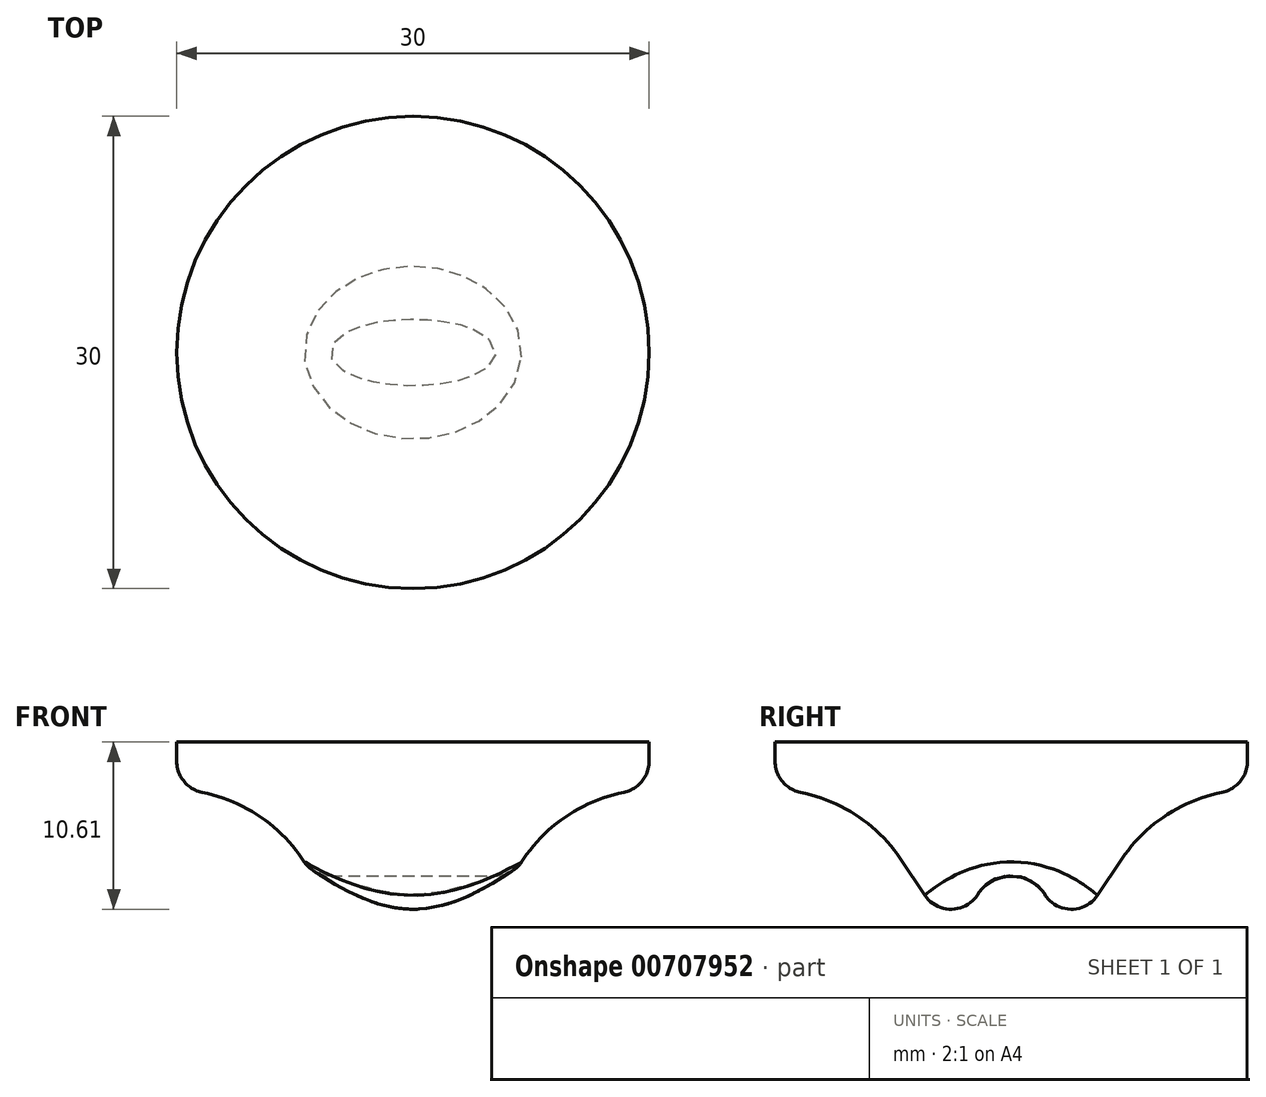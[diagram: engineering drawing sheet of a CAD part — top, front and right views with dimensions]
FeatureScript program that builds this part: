
annotation { "Feature Type Name" : "Feature", "Feature Type Description" : "" }
export const myFeature = defineFeature(function(context is Context, id is Id, definition is map)
    precondition{}
    {
        {
            var Q0;
            Q0=qCreatedBy(makeId("Front.planeOp"),FACE);
            var sketch = newSketch(context, id + "F0", { "sketchPlane" : qUnion([Q0])});
            skLineSegment(sketch, "E0", {"start": v(0, 0) * mm, "end": v(-15, 0) * mm});
            skLineSegment(sketch, "E1", {"start": v(-15, 0) * mm, "end": v(-15, -3) * mm});
            skLineSegment(sketch, "E2", {"start": v(-15, -3) * mm, "end": v(-10, -3) * mm});
            skLineSegment(sketch, "E3", {"start": v(-10, -3) * mm, "end": v(-2.62, -13.99) * mm});
            skLineSegment(sketch, "E4", {"start": v(0, -13.99) * mm, "end": v(-2.62, -13.99) * mm});
            skLineSegment(sketch, "E5", {"start": v(0, -13.99) * mm, "end": v(0, 0) * mm});
            skSolve(sketch);
        }
        {
            var Q0;
            Q0=makeQuery(id+"F0.imprint","IMPRINT",FACE,{"disambiguationData":[TD([[makeQuery(id+"F0.imprint","IMPRINT",EDGE,{"derivedFrom":sQuery(id+"F0.wireOp",EDGE,"E0")}),1.0]])]});
            var Q1;
            Q1=sQuery(id+"F0.wireOp",EDGE,"E5");
            revolve(context, id + "F1", {"surfaceOperationType" : NewSurfaceOperationType.NEW, "entities" : qUnion([Q0]), "axis" : qUnion([Q1]), "revolveType" : RevolveType.FULL});
        }
        {
            var Q0;
            Q0=makeQuery(id+"F1.opRevolve","SWEPT_EDGE",EDGE,{"disambiguationData":[OSD([sQuery(id+"F0.wireOp",EDGE,"E2"),sQuery(id+"F0.wireOp",EDGE,"E3")])]});
            fillet(context, id + "F2", {"entities" : qUnion([Q0]), "radius" : 10 * mm, "tangentPropagation" : true, "allowEdgeOverflow" : false});
        }
        {
            var Q0;
            Q0=makeQuery(id+"F2.opFillet","BLEND_EDGE",EDGE,{"blendedFrom":[makeQuery(id+"F1.opRevolve","SWEPT_EDGE",EDGE,{"disambiguationData":[OSD([sQuery(id+"F0.wireOp",EDGE,"E2"),sQuery(id+"F0.wireOp",EDGE,"E3")])]}),makeQuery(id+"F1.opRevolve","SWEPT_FACE",FACE,{"disambiguationData":[OSD([sQuery(id+"F0.wireOp",EDGE,"E1")])]})],"blendedInto":[makeQuery(id+"F1.opRevolve","SWEPT_FACE",FACE,{"disambiguationData":[OSD([sQuery(id+"F0.wireOp",EDGE,"E1")])]})]});
            fillet(context, id + "F3", {"entities" : qUnion([Q0]), "radius" : 2 * mm, "tangentPropagation" : true, "allowEdgeOverflow" : false});
        }
        {
            var Q0;
            Q0=makeQuery(id+"F1.opRevolve","SWEPT_EDGE",EDGE,{"disambiguationData":[OSD([sQuery(id+"F0.wireOp",EDGE,"E3"),sQuery(id+"F0.wireOp",EDGE,"E4")])]});
            fillet(context, id + "F4", {"entities" : qUnion([Q0]), "radius" : 3 * mm, "tangentPropagation" : true, "allowEdgeOverflow" : false});
        }
        {
            var Q0;
            Q0=qCreatedBy(makeId("Right.planeOp"),FACE);
            var sketch = newSketch(context, id + "F5", { "sketchPlane" : qUnion([Q0])});
            skArc(sketch, "E6", {"start": v(1.5, -12.99) * mm, "mid": v(0, -8.49) * mm, "end": v(-1.5, -12.99) * mm});
            skLineSegment(sketch, "E7", {"start": v(-1.5, -12.99) * mm, "end": v(-1.5, -14.62) * mm});
            skLineSegment(sketch, "E8", {"start": v(1.5, -12.99) * mm, "end": v(1.5, -14.62) * mm});
            skLineSegment(sketch, "E9", {"start": v(-1.5, -14.62) * mm, "end": v(1.5, -14.62) * mm});
            skSolve(sketch);
        }
        {
            var Q0;
            Q0=makeQuery(id+"F5.imprint","IMPRINT",FACE,{"disambiguationData":[TD([[makeQuery(id+"F5.imprint","IMPRINT",EDGE,{"derivedFrom":sQuery(id+"F5.wireOp",EDGE,"E6")}),1.0]])]});
            extrude(context, id + "F6", {"entities" : qUnion([Q0]), "operationType" : NewBodyOperationType.REMOVE, "endBound" : BoundingType.THROUGH_ALL, "oppositeDirection" : true, "depth" : 25 * mm, "offsetDistance" : 25 * mm, "hasSecondDirection" : true, "secondDirectionBound" : SecondDirectionBoundingType.THROUGH_ALL, "secondDirectionOppositeDirection" : false, "secondDirectionDepth" : 25 * mm});
        }
        {
            var Q0;
            Q0=makeQuery(id+"F6.boolean.opBoolean","COPY",EDGE,{"derivedFrom":makeQuery(id+"F6.opExtrude","SWEPT_EDGE",EDGE,{"disambiguationData":[OSD([sQuery(id+"F5.wireOp",EDGE,"E6"),sQuery(id+"F5.wireOp",EDGE,"E7")])]})});
            var Q1;
            Q1=makeQuery(id+"F6.boolean.opBoolean","COPY",EDGE,{"derivedFrom":makeQuery(id+"F6.opExtrude","SWEPT_EDGE",EDGE,{"disambiguationData":[OSD([sQuery(id+"F5.wireOp",EDGE,"E6"),sQuery(id+"F5.wireOp",EDGE,"E8")])]})});
            fillet(context, id + "F7", {"entities" : qUnion([Q0, Q1]), "radius" : 3 * mm, "tangentPropagation" : true, "allowEdgeOverflow" : false});
        }
        {
            var Q0;
            Q0=makeQuery(id+"F6.boolean.opBoolean","INTERSECT",EDGE,{"disambiguationData":[OD(0.0)],"derivedFrom":[makeQuery(id+"F1.opRevolve","SWEPT_FACE",FACE,{"disambiguationData":[OSD([sQuery(id+"F0.wireOp",EDGE,"E3")])]}),makeQuery(id+"F6.opExtrude","SWEPT_FACE",FACE,{"disambiguationData":[OSD([sQuery(id+"F5.wireOp",EDGE,"E6")])]})]});
            var Q1;
            Q1=makeQuery(id+"F7.opFillet","BLEND_EDGE",EDGE,{"disambiguationData":[OD(0.0)],"blendedFrom":[makeQuery(id+"F6.boolean.opBoolean","COPY",EDGE,{"derivedFrom":makeQuery(id+"F6.opExtrude","SWEPT_EDGE",EDGE,{"disambiguationData":[OSD([sQuery(id+"F5.wireOp",EDGE,"E6"),sQuery(id+"F5.wireOp",EDGE,"E7")])]})}),makeQuery(id+"F1.opRevolve","SWEPT_FACE",FACE,{"disambiguationData":[OSD([sQuery(id+"F0.wireOp",EDGE,"E3")])]})],"blendedInto":[makeQuery(id+"F1.opRevolve","SWEPT_FACE",FACE,{"disambiguationData":[OSD([sQuery(id+"F0.wireOp",EDGE,"E3")])]})]});
            var Q2;
            {var subQ0=sQuery(id+"F0.wireOp",EDGE,"E3");var subQ1=sQuery(id+"F5.wireOp",EDGE,"E7");Q2=makeQuery(id+"F7.opFillet","BLEND_EDGE",EDGE,{"disambiguationData":[OD(0.0)],"blendedFrom":[makeQuery(id+"F6.boolean.opBoolean","COPY",EDGE,{"derivedFrom":makeQuery(id+"F6.opExtrude","SWEPT_EDGE",EDGE,{"disambiguationData":[OSD([sQuery(id+"F5.wireOp",EDGE,"E6"),subQ1])]})}),makeQuery(id+"F6.boolean.opBoolean","SPLIT",FACE,{"disambiguationData":[TD([makeQuery(id+"F6.opExtrude","SWEPT_FACE",FACE,{"disambiguationData":[OSD([subQ1])]})])],"derivedFrom":makeQuery(id+"F4.opFillet","BLEND_FACE",FACE,{"disambiguationData":[OSD([subQ0,sQuery(id+"F0.wireOp",EDGE,"E4")])]})})],"blendedInto":[makeQuery(id+"F6.boolean.opBoolean","SPLIT",FACE,{"disambiguationData":[TD([makeQuery(id+"F6.opExtrude","SWEPT_FACE",FACE,{"disambiguationData":[OSD([subQ1])]})])],"derivedFrom":makeQuery(id+"F4.opFillet","BLEND_FACE",FACE,{"disambiguationData":[OSD([subQ0,sQuery(id+"F0.wireOp",EDGE,"E4")])]})})]});}
            var Q3;
            Q3=makeQuery(id+"F7.opFillet","BLEND_EDGE",EDGE,{"disambiguationData":[OD(1.0)],"blendedFrom":[makeQuery(id+"F6.boolean.opBoolean","COPY",EDGE,{"derivedFrom":makeQuery(id+"F6.opExtrude","SWEPT_EDGE",EDGE,{"disambiguationData":[OSD([sQuery(id+"F5.wireOp",EDGE,"E6"),sQuery(id+"F5.wireOp",EDGE,"E7")])]})}),makeQuery(id+"F1.opRevolve","SWEPT_FACE",FACE,{"disambiguationData":[OSD([sQuery(id+"F0.wireOp",EDGE,"E3")])]})],"blendedInto":[makeQuery(id+"F1.opRevolve","SWEPT_FACE",FACE,{"disambiguationData":[OSD([sQuery(id+"F0.wireOp",EDGE,"E3")])]})]});
            var Q4;
            Q4=makeQuery(id+"F6.boolean.opBoolean","INTERSECT",EDGE,{"disambiguationData":[OD(1.0)],"derivedFrom":[makeQuery(id+"F1.opRevolve","SWEPT_FACE",FACE,{"disambiguationData":[OSD([sQuery(id+"F0.wireOp",EDGE,"E3")])]}),makeQuery(id+"F6.opExtrude","SWEPT_FACE",FACE,{"disambiguationData":[OSD([sQuery(id+"F5.wireOp",EDGE,"E6")])]})]});
            var Q5;
            {var subQ0=sQuery(id+"F0.wireOp",EDGE,"E3");var subQ1=sQuery(id+"F5.wireOp",EDGE,"E8");Q5=makeQuery(id+"F7.opFillet","BLEND_EDGE",EDGE,{"disambiguationData":[OD(0.0)],"blendedFrom":[makeQuery(id+"F6.boolean.opBoolean","COPY",EDGE,{"derivedFrom":makeQuery(id+"F6.opExtrude","SWEPT_EDGE",EDGE,{"disambiguationData":[OSD([sQuery(id+"F5.wireOp",EDGE,"E6"),subQ1])]})}),makeQuery(id+"F6.boolean.opBoolean","SPLIT",FACE,{"disambiguationData":[TD([makeQuery(id+"F6.opExtrude","SWEPT_FACE",FACE,{"disambiguationData":[OSD([subQ1])]})])],"derivedFrom":makeQuery(id+"F4.opFillet","BLEND_FACE",FACE,{"disambiguationData":[OSD([subQ0,sQuery(id+"F0.wireOp",EDGE,"E4")])]})})],"blendedInto":[makeQuery(id+"F6.boolean.opBoolean","SPLIT",FACE,{"disambiguationData":[TD([makeQuery(id+"F6.opExtrude","SWEPT_FACE",FACE,{"disambiguationData":[OSD([subQ1])]})])],"derivedFrom":makeQuery(id+"F4.opFillet","BLEND_FACE",FACE,{"disambiguationData":[OSD([subQ0,sQuery(id+"F0.wireOp",EDGE,"E4")])]})})]});}
            var Q6;
            Q6=makeQuery(id+"F7.opFillet","BLEND_EDGE",EDGE,{"disambiguationData":[OD(0.0)],"blendedFrom":[makeQuery(id+"F6.boolean.opBoolean","COPY",EDGE,{"derivedFrom":makeQuery(id+"F6.opExtrude","SWEPT_EDGE",EDGE,{"disambiguationData":[OSD([sQuery(id+"F5.wireOp",EDGE,"E6"),sQuery(id+"F5.wireOp",EDGE,"E8")])]})}),makeQuery(id+"F1.opRevolve","SWEPT_FACE",FACE,{"disambiguationData":[OSD([sQuery(id+"F0.wireOp",EDGE,"E3")])]})],"blendedInto":[makeQuery(id+"F1.opRevolve","SWEPT_FACE",FACE,{"disambiguationData":[OSD([sQuery(id+"F0.wireOp",EDGE,"E3")])]})]});
            var Q7;
            Q7=makeQuery(id+"F6.boolean.opBoolean","INTERSECT",EDGE,{"derivedFrom":[makeQuery(id+"F4.opFillet","BLEND_FACE",FACE,{"disambiguationData":[OSD([sQuery(id+"F0.wireOp",EDGE,"E3"),sQuery(id+"F0.wireOp",EDGE,"E4")])]}),makeQuery(id+"F6.opExtrude","SWEPT_FACE",FACE,{"disambiguationData":[OSD([sQuery(id+"F5.wireOp",EDGE,"E8")])]})]});
            var Q8;
            {var subQ0=sQuery(id+"F0.wireOp",EDGE,"E3");var subQ1=sQuery(id+"F5.wireOp",EDGE,"E8");Q8=makeQuery(id+"F7.opFillet","BLEND_EDGE",EDGE,{"disambiguationData":[OD(1.0)],"blendedFrom":[makeQuery(id+"F6.boolean.opBoolean","COPY",EDGE,{"derivedFrom":makeQuery(id+"F6.opExtrude","SWEPT_EDGE",EDGE,{"disambiguationData":[OSD([sQuery(id+"F5.wireOp",EDGE,"E6"),subQ1])]})}),makeQuery(id+"F6.boolean.opBoolean","SPLIT",FACE,{"disambiguationData":[TD([makeQuery(id+"F6.opExtrude","SWEPT_FACE",FACE,{"disambiguationData":[OSD([subQ1])]})])],"derivedFrom":makeQuery(id+"F4.opFillet","BLEND_FACE",FACE,{"disambiguationData":[OSD([subQ0,sQuery(id+"F0.wireOp",EDGE,"E4")])]})})],"blendedInto":[makeQuery(id+"F6.boolean.opBoolean","SPLIT",FACE,{"disambiguationData":[TD([makeQuery(id+"F6.opExtrude","SWEPT_FACE",FACE,{"disambiguationData":[OSD([subQ1])]})])],"derivedFrom":makeQuery(id+"F4.opFillet","BLEND_FACE",FACE,{"disambiguationData":[OSD([subQ0,sQuery(id+"F0.wireOp",EDGE,"E4")])]})})]});}
            var Q9;
            Q9=makeQuery(id+"F7.opFillet","BLEND_EDGE",EDGE,{"disambiguationData":[OD(1.0)],"blendedFrom":[makeQuery(id+"F6.boolean.opBoolean","COPY",EDGE,{"derivedFrom":makeQuery(id+"F6.opExtrude","SWEPT_EDGE",EDGE,{"disambiguationData":[OSD([sQuery(id+"F5.wireOp",EDGE,"E6"),sQuery(id+"F5.wireOp",EDGE,"E8")])]})}),makeQuery(id+"F1.opRevolve","SWEPT_FACE",FACE,{"disambiguationData":[OSD([sQuery(id+"F0.wireOp",EDGE,"E3")])]})],"blendedInto":[makeQuery(id+"F1.opRevolve","SWEPT_FACE",FACE,{"disambiguationData":[OSD([sQuery(id+"F0.wireOp",EDGE,"E3")])]})]});
            var Q10;
            {var subQ0=sQuery(id+"F0.wireOp",EDGE,"E3");var subQ1=sQuery(id+"F5.wireOp",EDGE,"E7");Q10=makeQuery(id+"F7.opFillet","BLEND_EDGE",EDGE,{"disambiguationData":[OD(1.0)],"blendedFrom":[makeQuery(id+"F6.boolean.opBoolean","COPY",EDGE,{"derivedFrom":makeQuery(id+"F6.opExtrude","SWEPT_EDGE",EDGE,{"disambiguationData":[OSD([sQuery(id+"F5.wireOp",EDGE,"E6"),subQ1])]})}),makeQuery(id+"F6.boolean.opBoolean","SPLIT",FACE,{"disambiguationData":[TD([makeQuery(id+"F6.opExtrude","SWEPT_FACE",FACE,{"disambiguationData":[OSD([subQ1])]})])],"derivedFrom":makeQuery(id+"F4.opFillet","BLEND_FACE",FACE,{"disambiguationData":[OSD([subQ0,sQuery(id+"F0.wireOp",EDGE,"E4")])]})})],"blendedInto":[makeQuery(id+"F6.boolean.opBoolean","SPLIT",FACE,{"disambiguationData":[TD([makeQuery(id+"F6.opExtrude","SWEPT_FACE",FACE,{"disambiguationData":[OSD([subQ1])]})])],"derivedFrom":makeQuery(id+"F4.opFillet","BLEND_FACE",FACE,{"disambiguationData":[OSD([subQ0,sQuery(id+"F0.wireOp",EDGE,"E4")])]})})]});}
            fillet(context, id + "F8", {"entities" : qUnion([Q0, Q1, Q2, Q3, Q4, Q5, Q6, Q7, Q8, Q9, Q10]), "radius" : 2 * mm, "tangentPropagation" : true, "allowEdgeOverflow" : false});
        }
    });
